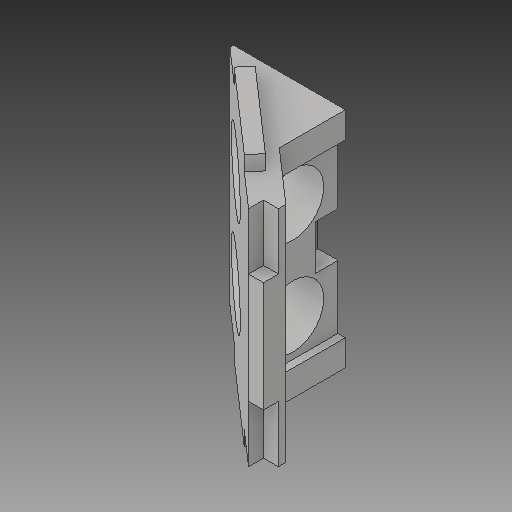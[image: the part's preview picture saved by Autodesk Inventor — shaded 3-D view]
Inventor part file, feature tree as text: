
AUTODESK INVENTOR PART (.ipt)
format: ipt  version: 2019 (Build 230136000, 136)  size: 190,464 bytes
history: native  units: mm
features: sketch x10, other x4, extrude x1, projected_geometry x1
ambient origin geometry x8: Origin, YZ Plane, XZ Plane, XY Plane, X Axis, Y Axis, Z Axis, Center Point
bodies: Body1 (feature_tree)
feature tree (16):
  other  "Sensor.ipt"
  extrude  "Выдавливание1"  Depth=10.0mm
  other  "Твердое тело1::Sensor.ipt"
  other  "Элемент создания тегов1"
  sketch  "Эскиз1"
  sketch  "Эскиз2"
  sketch  "Эскиз3"
  sketch  "Эскиз4"
  sketch  "Эскиз5"
  sketch  "Эскиз6"
  sketch  "Эскиз7"
  sketch  "Эскиз8"
  sketch  "Эскиз9"
  sketch  "Эскиз10"
  projected_geometry  "Спроецированная петля1"
  other  "Твердое тело1"
